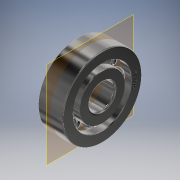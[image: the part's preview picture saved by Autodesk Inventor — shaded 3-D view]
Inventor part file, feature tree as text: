
AUTODESK INVENTOR PART (.ipt)
format: ipt  version: 2018 (Build 220112000, 112)  size: 531,968 bytes
history: native  units: mm
features: plane x1, other x1
ambient origin geometry x8: Origin, YZ Plane, XZ Plane, XY Plane, X Axis, Y Axis, Z Axis, Center Point
bodies: Solid1 (feature_tree)
feature tree (2):
  plane  "Work Plane1"
  other  "Wrap1"
